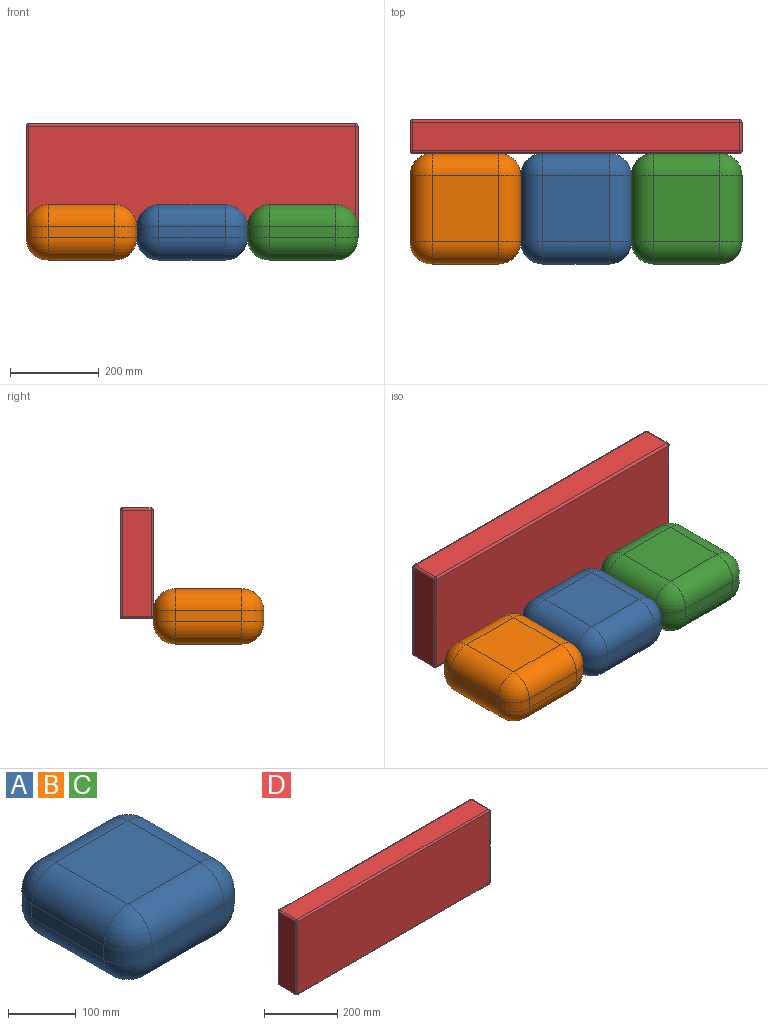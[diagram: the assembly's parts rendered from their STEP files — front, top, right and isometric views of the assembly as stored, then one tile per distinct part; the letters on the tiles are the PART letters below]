
ASSEMBLY  parts=4 mates=3
PART A: 26 faces, bbox 250x250x125 mm
  f0: plane 150x25mm, normal (-1,0,0), area 3750mm2, adj f14,f19,f22,f25
  f1: plane 150x150mm, normal (0,0,-1), area 22500mm2, adj f11,f20,f21,f25
  f2: plane 150x25mm, normal (1,0,0), area 3750mm2, adj f6,f10,f11,f12
  f3: plane 150x150mm, normal (0,0,1), area 22500mm2, adj f6,f9,f13,f14
  f4: plane 150x25mm, normal (0,-1,0), area 3750mm2, adj f9,f10,f19,f20
  f5: plane 150x25mm, normal (0,1,0), area 3750mm2, adj f12,f13,f21,f22
  f6: cylinder r=50mm len=150mm, axis (0,1,0), area 11781mm2, adj f2,f3,f7,f8
  f7: sphere r=50mm, area 3927mm2, adj f6,f9,f10
  f8: sphere r=50mm, area 3927mm2, adj f6,f12,f13
  f9: cylinder r=50mm len=150mm, axis (1,0,0), area 11781mm2, adj f3,f4,f7,f15
  f10: cylinder r=50mm len=50mm, axis (0,0,-1), area 1963.5mm2, adj f2,f4,f7,f16
  f11: cylinder r=50mm len=150mm, axis (0,-1,0), area 11781mm2, adj f1,f2,f16,f17
  f12: cylinder r=50mm len=50mm, axis (0,0,1), area 1963.5mm2, adj f2,f5,f8,f17
  f13: cylinder r=50mm len=150mm, axis (-1,0,0), area 11781mm2, adj f3,f5,f8,f18
  f14: cylinder r=50mm len=150mm, axis (0,-1,0), area 11781mm2, adj f0,f3,f15,f18
  f15: sphere r=50mm, area 3927mm2, adj f9,f14,f19
  f16: sphere r=50mm, area 3927mm2, adj f10,f11,f20
  f17: sphere r=50mm, area 3927mm2, adj f11,f12,f21
  f18: sphere r=50mm, area 3927mm2, adj f13,f14,f22
  f19: cylinder r=50mm len=50mm, axis (0,0,1), area 1963.5mm2, adj f0,f4,f15,f23
  f20: cylinder r=50mm len=150mm, axis (-1,0,0), area 11781mm2, adj f1,f4,f16,f23
  f21: cylinder r=50mm len=150mm, axis (1,0,0), area 11781mm2, adj f1,f5,f17,f24
  f22: cylinder r=50mm len=50mm, axis (0,0,-1), area 1963.5mm2, adj f0,f5,f18,f24
  f23: sphere r=50mm, area 3927mm2, adj f19,f20,f25
  f24: sphere r=50mm, area 3927mm2, adj f21,f22,f25
  f25: cylinder r=50mm len=150mm, axis (0,1,0), area 11781mm2, adj f0,f1,f23,f24
PART B: same geometry as A
PART C: same geometry as A
PART D: 26 faces, bbox 750x75x250 mm
  f0: plane 240x65mm, normal (1,0,0), area 15600mm2, adj f14,f19,f22,f25
  f1: plane 740x65mm, normal (0,0,1), area 48100mm2, adj f11,f20,f21,f25
  f2: plane 240x65mm, normal (-1,0,0), area 15600mm2, adj f6,f10,f11,f12
  f3: plane 740x65mm, normal (0,0,-1), area 48100mm2, adj f6,f9,f13,f14
  f4: plane 740x240mm, normal (0,-1,0), area 177600mm2, adj f9,f10,f19,f20
  f5: plane 740x240mm, normal (0,1,0), area 177600mm2, adj f12,f13,f21,f22
  f6: cylinder r=5mm len=65mm, axis (0,1,0), area 510.5mm2, adj f2,f3,f7,f8
  f7: sphere r=5mm, area 39.3mm2, adj f6,f9,f10
  f8: sphere r=5mm, area 39.3mm2, adj f6,f12,f13
  f9: cylinder r=5mm len=740mm, axis (-1,0,0), area 5811.9mm2, adj f3,f4,f7,f15
  f10: cylinder r=5mm len=240mm, axis (0,0,1), area 1885mm2, adj f2,f4,f7,f16
  f11: cylinder r=5mm len=65mm, axis (0,-1,0), area 510.5mm2, adj f1,f2,f16,f17
  f12: cylinder r=5mm len=240mm, axis (0,0,-1), area 1885mm2, adj f2,f5,f8,f17
  f13: cylinder r=5mm len=740mm, axis (1,0,0), area 5811.9mm2, adj f3,f5,f8,f18
  f14: cylinder r=5mm len=65mm, axis (0,-1,0), area 510.5mm2, adj f0,f3,f15,f18
  f15: sphere r=5mm, area 39.3mm2, adj f9,f14,f19
  f16: sphere r=5mm, area 39.3mm2, adj f10,f11,f20
  f17: sphere r=5mm, area 39.3mm2, adj f11,f12,f21
  f18: sphere r=5mm, area 39.3mm2, adj f13,f14,f22
  f19: cylinder r=5mm len=240mm, axis (0,0,-1), area 1885mm2, adj f0,f4,f15,f23
  f20: cylinder r=5mm len=740mm, axis (1,0,0), area 5811.9mm2, adj f1,f4,f16,f23
  f21: cylinder r=5mm len=740mm, axis (-1,0,0), area 5811.9mm2, adj f1,f5,f17,f24
  f22: cylinder r=5mm len=240mm, axis (0,0,1), area 1885mm2, adj f0,f5,f18,f24
  f23: sphere r=5mm, area 39.3mm2, adj f19,f20,f25
  f24: sphere r=5mm, area 39.3mm2, adj f21,f22,f25
  f25: cylinder r=5mm len=65mm, axis (0,1,0), area 510.5mm2, adj f0,f1,f23,f24
PLACE A at identity fixed
PLACE B t=(-250,0,0)mm
PLACE C t=(250,0,0)mm
PLACE D t=(0,162.5,120)mm
MATE fastened A.f5 <-> D.f4  axis (0,1,0) through (0,125,0)mm
MATE fastened B.f2 <-> A.f0  axis (1,0,0) through (-125,0,0)mm
MATE fastened C.f0 <-> A.f2  axis (-1,0,0) through (125,0,0)mm
